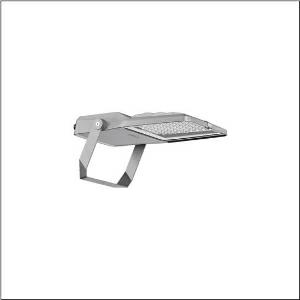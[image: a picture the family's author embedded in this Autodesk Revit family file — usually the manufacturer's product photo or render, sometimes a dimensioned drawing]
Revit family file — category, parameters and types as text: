
# Revit family: floodlight_fl_21_iq_mini___pl43_5xa7771d4a1a_5f3b
name_source: partatom
category: Lighting Fixtures
units: mm (PartAtom-declared; Revit-internal decimal feet)

## family parameters
Cut with Voids When Loaded = No
Host = Face
Light Source = No
Part Type = Normal
Room Calculation Point = No
Round Connector Dimension = Use Diameter
Shared = No

## types (1)
- --- (1 x LED, 19090 lm, 143 W, 4000K)
    Apparent Load = 143 VA
    CIE Flux Codes = 27 78 99 100 100
    Color Rendering = 70
    Color Temperature = 4000K
    Default Elevation = 1800 mm
    Description = Floodlight FL 21 iQ mini, floodlight, primary light control with lens, of PMMA, primary optical cover: protective disc, of toughened safety glass, transparent, light distribution: PL43, light emission: direct distribution, installation type: surface-mounted, lamps: LED, High Power LED, rated values: 19.090lm | 143W | 133,5lm/W (begin service life); end service life: 19.090lm | 151,6W; at 50% lumin. flux: 9.545lm | 60,8W | 157lm/W, colour temperature: 4000K, colour rendering: CRI > 70, light colour: 740, light setting 1 begin service life: 100% | 19.090lm | 143W | 133,5lm/W | 4.000K, light setting 1 end service life: 151,6W, further light settings possible, control: Auto-Match, Temp-Guard, Lumen-Switch, Night-Set, Smart-Wire, Light-Fading, Desk-Remote (wireless, voltage-free reading and setting of iQ features in the workshop via application-optimized NFC function/RFID function), optimised constant luminous flux control (CLO 2.0), pre-setting: linear dimming characteristic, with terminal, 6-pole, mains connection: 220..240V, AC, 50/60Hz, luminaire housing, of diecast aluminium, powder-coated, SITECO metallic grey (DB 702S), corrosivity category C5 mid according to DIN EN ISO 12944suitable for swimming poolschlorine-resistant, sealing non-destructively replaceable, mounting bracket, of steel, galvanised, powder-coated, SITECO metallic grey (DB 702S), protection rating (complete): IP66, insulation class (complete): insulation class II (safety insulation), certification: CE, ENEC, VDE, protection symbol: D, impact resistance: IK08, permissible operating ambient temperature: -40..+40°C, permissible operating ambient temperature for outdoor applications: -40..+50°C, standard: DIN EN 12944, LABS conformity tested according to VDMA 24364:2018-05, packaging unit: 1 piece

Light Distribution: PL43
    Height = 70 mm
    Lamp = 1 x LED
    Lamp Light Flux = 19090 lm
    Lamp Power = 143 W
    Lamp count = 1
    Length = 485 mm
    Luminous efficacy = 133 lm/W
    Manufacturer = Siteco
    ModVariant = No
    Model = 5XA7771D4A1A
    Number of Poles = 1
    OnlyDefault = Yes
    Power Factor = 1
    Product Name = Floodlight FL 21 iQ mini | PL43
    Product group = floodlight | pylon annexe
    ProductGroupID = 6201
    Protection Class = Protection class II
    Protection Degree = IP 66
    RLX_Detail_Level = 1
    RLX_Emergency_Light_Flux = 0 lm
    RLX_Emergency_Type = 0
    RLX_Emergency_Type_DB = No
    RlxData = <blob elided: 96649 chars, md5=8604ae45>
    Socket = socket
    Standby Power = 0 W
    System Light Flux = 19090 lm
    System Power = 143 W
    Type Comments = factory setting: luminous flux: 100 % | dim-lin: 254 | 730 mA
    Type Image = l_1006845.jpg
    URL = http://relux.com
    VarID = @adj_160859
    Voltage = 0 V
    Weight = 0.00 kg
    Width = 337 mm

## geometry (parser evidence)
native form markers: Blend x4, Sweep x12
no freeform markers — native parametric forms only
